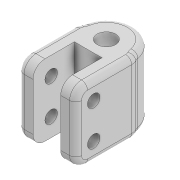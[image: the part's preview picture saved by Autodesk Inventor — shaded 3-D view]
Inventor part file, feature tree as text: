
AUTODESK INVENTOR PART (.ipt)
format: ipt  version: 2022 (Build 260153000, 153)  size: 214,528 bytes
history: native  units: mm
features: extrude x4, sketch x3, fillet x3
ambient origin geometry x8: Origin, YZ Plane, XZ Plane, XY Plane, X Axis, Y Axis, Z Axis, Center Point
bodies: Solid1 (feature_tree)
feature tree (10):
  extrude  "Extrusion1"  Depth=9.0mm
  sketch  "Sketch2"  dims[d2=12.0mm d3=0.0mm d4=4.65mm]
  extrude  "Extrusion2"  Depth=4.65mm
  extrude  "Extrusion4"  Depth=2.5mm
  extrude  "Extrusion3"  Depth=2.5mm
  fillet  "Fillet2"  Radius=10.0mm
  fillet  "Fillet3"  Radius=12.0mm
  fillet  "Fillet4"  Radius=2.1mm
  sketch  "Sketch1"  dims[d0=3.1mm d1=9.0mm]
  sketch  "Sketch3"  dims[d5=2.325mm d6=2.5mm d7=2.5mm d8=10.0mm d9=12.0mm d10=0.0mm d11=2.1mm d12=2.1mm d13=2.0mm d14=2.0mm d17=11.0mm d18=0.0mm d20=2.0mm d21=2.0mm d22=1.0mm d23=20.0mm d24=0.0mm d25=1.5mm d26=5.9mm d27=3.05mm]
